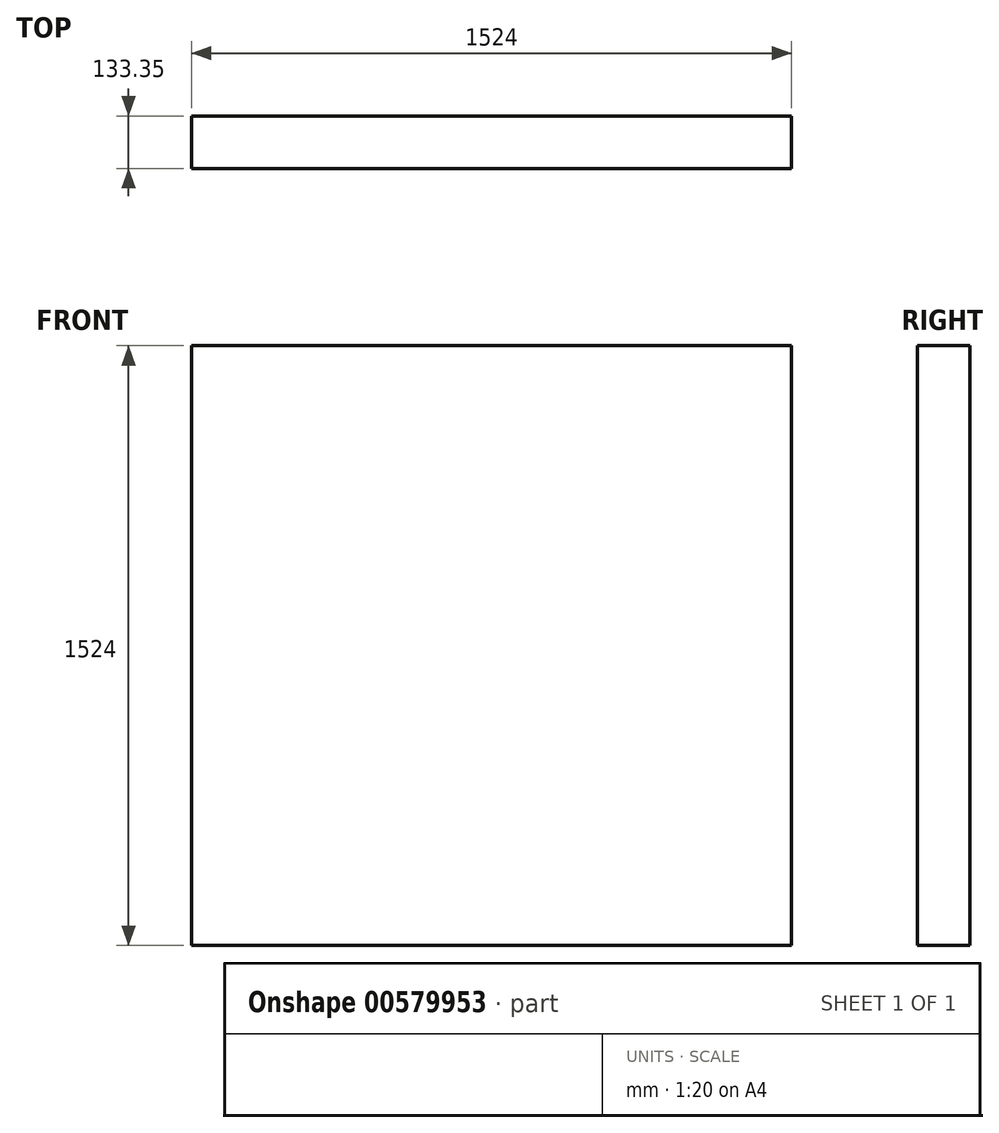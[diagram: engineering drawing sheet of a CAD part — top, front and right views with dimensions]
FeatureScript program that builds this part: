
annotation { "Feature Type Name" : "Feature", "Feature Type Description" : "" }
export const myFeature = defineFeature(function(context is Context, id is Id, definition is map)
    precondition{}
    {
        {
            var Q0;
            Q0=qCreatedBy(makeId("Front.planeOp"),FACE);
            var sketch = newSketch(context, id + "F0", { "sketchPlane" : qUnion([Q0])});
            skLineSegment(sketch, "E0.bottom", {"start": v(-788.13, 861) * mm, "end": v(735.87, 861) * mm});
            skLineSegment(sketch, "E0.top", {"start": v(-788.13, -663) * mm, "end": v(735.87, -663) * mm});
            skLineSegment(sketch, "E0.left", {"start": v(-788.13, 861) * mm, "end": v(-788.13, -663) * mm});
            skLineSegment(sketch, "E0.right", {"start": v(735.87, 861) * mm, "end": v(735.87, -663) * mm});
            skSolve(sketch);
        }
        {
            var Q0;
            Q0=makeQuery(id+"F0.imprint","IMPRINT",FACE,{"disambiguationData":[TD([[makeQuery(id+"F0.imprint","IMPRINT",EDGE,{"derivedFrom":sQuery(id+"F0.wireOp",EDGE,"E0.bottom")}),-1.0]])]});
            extrude(context, id + "F1", {"entities" : qUnion([Q0]), "depth" : 133.35 * mm, "offsetDistance" : 25.4 * mm});
        }
    });
